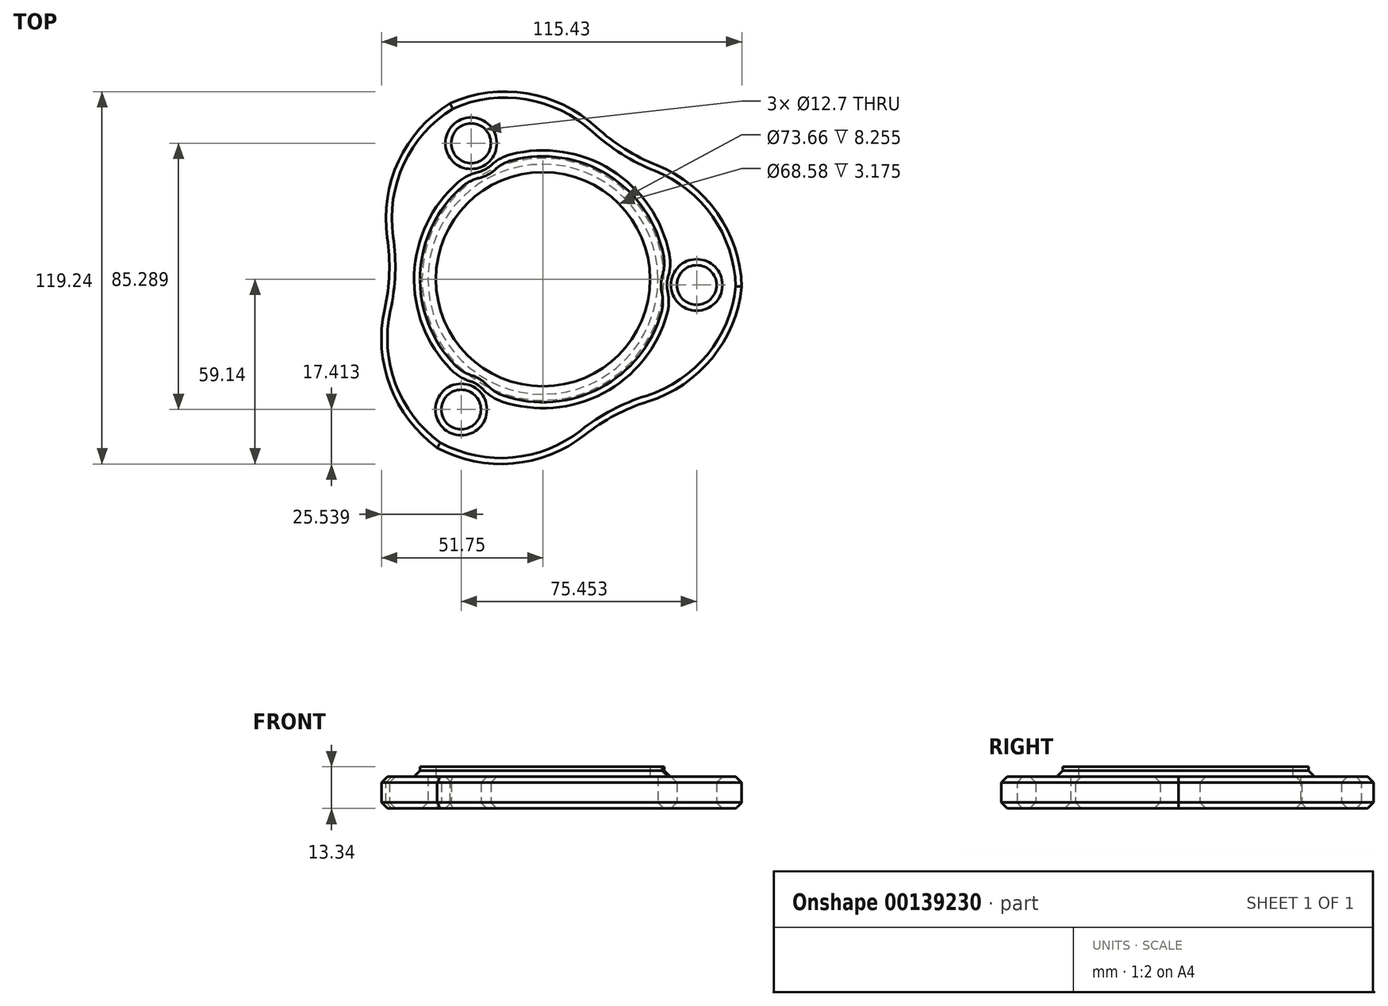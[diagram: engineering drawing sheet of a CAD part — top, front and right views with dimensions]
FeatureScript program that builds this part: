
annotation { "Feature Type Name" : "Feature", "Feature Type Description" : "" }
export const myFeature = defineFeature(function(context is Context, id is Id, definition is map)
    precondition{}
    {
        {
            var Q0;
            Q0=qCreatedBy(makeId("Top.planeOp"),FACE);
            var sketch = newSketch(context, id + "F0", { "sketchPlane" : qUnion([Q0])});
            skCircle(sketch, "E0", {"center": v(0, 0) * mm, "radius": 49.28 * mm, "construction": true});
            skCircle(sketch, "E1", {"center": v(-23.03, 43.56) * mm, "radius": 6.35 * mm});
            skCircle(sketch, "E2.1.0", {"center": v(-26.21, -41.73) * mm, "radius": 6.35 * mm});
            skCircle(sketch, "E2.2.0", {"center": v(49.24, -1.84) * mm, "radius": 6.35 * mm});
            skCircle(sketch, "E3", {"center": v(0, 0) * mm, "radius": 36.83 * mm});
            skArc(sketch, "E4.0", {"start": v(-9.12, 48.42) * mm, "mid": v(-17.65, 57.28) * mm, "end": v(-29.92, 56.59) * mm, "construction": true});
            skLineSegment(sketch, "E5", {"start": v(-26.21, -41.73) * mm, "end": v(0, 0) * mm, "construction": true});
            skLineSegment(sketch, "E6", {"start": v(0, 0) * mm, "end": v(59.82, 95.22) * mm, "construction": true});
            skArc(sketch, "E7", {"start": v(5, 63.81) * mm, "mid": v(-29.92, 56.59) * mm, "end": v(-55.55, 31.8) * mm});
            skArc(sketch, "E8", {"start": v(5, 63.81) * mm, "mid": v(26.21, 41.73) * mm, "end": v(55.31, 32.2) * mm});
            skArc(sketch, "E9.1.0", {"start": v(-57.76, -27.57) * mm, "mid": v(-49.24, 1.84) * mm, "end": v(-55.55, 31.8) * mm});
            skArc(sketch, "E9.2.0", {"start": v(52.76, -36.24) * mm, "mid": v(23.03, -43.56) * mm, "end": v(0.24, -64) * mm});
            skArc(sketch, "E10.trimOffspring", {"start": v(-57.76, -27.57) * mm, "mid": v(-34.05, -54.2) * mm, "end": v(0.24, -64) * mm});
            skArc(sketch, "E11.trimOffspring", {"start": v(52.76, -36.24) * mm, "mid": v(63.96, -2.39) * mm, "end": v(55.31, 32.2) * mm});
            skSolve(sketch);
        }
        {
            var Q0;
            Q0=makeQuery(id+"F0.imprint","IMPRINT",FACE,{"disambiguationData":[TD([[makeQuery(id+"F0.imprint","IMPRINT",EDGE,{"derivedFrom":sQuery(id+"F0.wireOp",EDGE,"E1")}),-1.0]])]});
            extrude(context, id + "F1", {"entities" : qUnion([Q0]), "depth" : 10.16 * mm});
        }
        {
            var Q0;
            Q0=makeQuery(id+"F1.opExtrude","SWEPT_EDGE",EDGE,{"disambiguationData":[OSD([sQuery(id+"F0.wireOp",EDGE,"E7"),sQuery(id+"F0.wireOp",EDGE,"E9.1.0")])]});
            var Q1;
            Q1=makeQuery(id+"F1.opExtrude","SWEPT_EDGE",EDGE,{"disambiguationData":[OSD([sQuery(id+"F0.wireOp",EDGE,"E9.1.0"),sQuery(id+"F0.wireOp",EDGE,"E10.trimOffspring")])]});
            var Q2;
            Q2=makeQuery(id+"F1.opExtrude","SWEPT_EDGE",EDGE,{"disambiguationData":[OSD([sQuery(id+"F0.wireOp",EDGE,"E9.2.0"),sQuery(id+"F0.wireOp",EDGE,"E10.trimOffspring")])]});
            var Q3;
            Q3=makeQuery(id+"F1.opExtrude","SWEPT_EDGE",EDGE,{"disambiguationData":[OSD([sQuery(id+"F0.wireOp",EDGE,"E9.2.0"),sQuery(id+"F0.wireOp",EDGE,"E11.trimOffspring")])]});
            var Q4;
            Q4=makeQuery(id+"F1.opExtrude","SWEPT_EDGE",EDGE,{"disambiguationData":[OSD([sQuery(id+"F0.wireOp",EDGE,"E7"),sQuery(id+"F0.wireOp",EDGE,"E8")])]});
            var Q5;
            Q5=makeQuery(id+"F1.opExtrude","SWEPT_EDGE",EDGE,{"disambiguationData":[OSD([sQuery(id+"F0.wireOp",EDGE,"E8"),sQuery(id+"F0.wireOp",EDGE,"E11.trimOffspring")])]});
            fillet(context, id + "F2", {"entities" : qUnion([Q0, Q1, Q2, Q3, Q4, Q5]), "radius" : 43.18 * mm, "tangentPropagation" : true, "allowEdgeOverflow" : false});
        }
        {
            var Q0;
            Q0=makeQuery(id+"F1.opExtrude","CAP_FACE",FACE,{"disambiguationData":[OSD([sQuery(id+"F0.wireOp",EDGE,"E1"),sQuery(id+"F0.wireOp",EDGE,"E2.1.0"),sQuery(id+"F0.wireOp",EDGE,"E2.2.0"),sQuery(id+"F0.wireOp",EDGE,"E3"),sQuery(id+"F0.wireOp",EDGE,"E7"),sQuery(id+"F0.wireOp",EDGE,"E8"),sQuery(id+"F0.wireOp",EDGE,"E9.1.0"),sQuery(id+"F0.wireOp",EDGE,"E9.2.0"),sQuery(id+"F0.wireOp",EDGE,"E10.trimOffspring"),sQuery(id+"F0.wireOp",EDGE,"E11.trimOffspring")])],"isStart":false});
            var sketch = newSketch(context, id + "F3", { "sketchPlane" : qUnion([Q0])});
            skCircle(sketch, "E12.0", {"center": v(0, 0) * mm, "radius": 34.3 * mm});
            skArc(sketch, "E13.0", {"start": v(-25.95, 29.6) * mm, "mid": v(-39.34, 1.47) * mm, "end": v(-28.08, -27.6) * mm});
            skArc(sketch, "E14.0", {"start": v(-20.45, 32.43) * mm, "mid": v(-17.69, 33.46) * mm, "end": v(-15.28, 35.16) * mm});
            skArc(sketch, "E15.0", {"start": v(38.3, 1.5) * mm, "mid": v(37.82, -1.41) * mm, "end": v(38.1, -4.34) * mm});
            skArc(sketch, "E16.0", {"start": v(-17.86, -33.92) * mm, "mid": v(-20.13, -32.05) * mm, "end": v(-22.8, -30.82) * mm});
            skArc(sketch, "E17.trimOffspring", {"start": v(38.62, 7.67) * mm, "mid": v(20.94, 33.34) * mm, "end": v(-9.85, 38.12) * mm});
            skArc(sketch, "E18.trimOffspring", {"start": v(-12.67, -37.28) * mm, "mid": v(18.4, -34.8) * mm, "end": v(37.94, -10.52) * mm});
            skPoint(sketch, "E19.visualSharp", {"position": v(-22.74, 32.14) * mm});
            skArc(sketch, "E19.filletArc", {"start": v(-20.45, 32.43) * mm, "mid": v(-23.37, 31.36) * mm, "end": v(-25.95, 29.6) * mm});
            skPoint(sketch, "E20.visualSharp", {"position": v(-13.75, 36.9) * mm});
            skArc(sketch, "E20.filletArc", {"start": v(-9.85, 38.12) * mm, "mid": v(-12.75, 36.97) * mm, "end": v(-15.28, 35.16) * mm});
            skPoint(sketch, "E21.visualSharp", {"position": v(39.2, 3.63) * mm});
            skArc(sketch, "E21.filletArc", {"start": v(38.3, 1.5) * mm, "mid": v(38.84, 4.56) * mm, "end": v(38.62, 7.67) * mm});
            skPoint(sketch, "E22.visualSharp", {"position": v(38.82, -6.54) * mm});
            skArc(sketch, "E22.filletArc", {"start": v(37.94, -10.52) * mm, "mid": v(38.4, -7.44) * mm, "end": v(38.1, -4.34) * mm});
            skPoint(sketch, "E23.visualSharp", {"position": v(-16.46, -35.76) * mm});
            skArc(sketch, "E23.filletArc", {"start": v(-17.86, -33.92) * mm, "mid": v(-15.47, -35.92) * mm, "end": v(-12.67, -37.28) * mm});
            skPoint(sketch, "E24.visualSharp", {"position": v(-25.07, -30.35) * mm});
            skArc(sketch, "E24.filletArc", {"start": v(-28.08, -27.6) * mm, "mid": v(-25.64, -29.53) * mm, "end": v(-22.8, -30.82) * mm});
            skSolve(sketch);
        }
        {
            var Q0;
            Q0 = qSketchRegion(id + "F3", true);
            extrude(context, id + "F4", {"entities" : qUnion([Q0]), "operationType" : NewBodyOperationType.ADD, "depth" : 3.17 * mm});
        }
        {
            var Q0;
            Q0=makeQuery(id+"F1.opExtrude","CAP_FACE",FACE,{"disambiguationData":[OSD([sQuery(id+"F0.wireOp",EDGE,"E1"),sQuery(id+"F0.wireOp",EDGE,"E2.1.0"),sQuery(id+"F0.wireOp",EDGE,"E2.2.0"),sQuery(id+"F0.wireOp",EDGE,"E3"),sQuery(id+"F0.wireOp",EDGE,"E7"),sQuery(id+"F0.wireOp",EDGE,"E8"),sQuery(id+"F0.wireOp",EDGE,"E9.1.0"),sQuery(id+"F0.wireOp",EDGE,"E9.2.0"),sQuery(id+"F0.wireOp",EDGE,"E10.trimOffspring"),sQuery(id+"F0.wireOp",EDGE,"E11.trimOffspring")])],"isStart":false});
            var Q1;
            Q1=makeQuery(id+"F1.opExtrude","CAP_FACE",FACE,{"disambiguationData":[OSD([sQuery(id+"F0.wireOp",EDGE,"E1"),sQuery(id+"F0.wireOp",EDGE,"E2.1.0"),sQuery(id+"F0.wireOp",EDGE,"E2.2.0"),sQuery(id+"F0.wireOp",EDGE,"E3"),sQuery(id+"F0.wireOp",EDGE,"E7"),sQuery(id+"F0.wireOp",EDGE,"E8"),sQuery(id+"F0.wireOp",EDGE,"E9.1.0"),sQuery(id+"F0.wireOp",EDGE,"E9.2.0"),sQuery(id+"F0.wireOp",EDGE,"E10.trimOffspring"),sQuery(id+"F0.wireOp",EDGE,"E11.trimOffspring")])],"isStart":true});
            var Q2;
            Q2=makeQuery(id+"F1.opExtrude","CAP_EDGE",EDGE,{"disambiguationData":[OSD([sQuery(id+"F0.wireOp",EDGE,"E3")])],"isStart":false});
            chamfer(context, id + "F5", {"entities" : qUnion([Q0, Q1, Q2]), "width" : 1.9 * mm, "tangentPropagation" : true});
        }
    });
